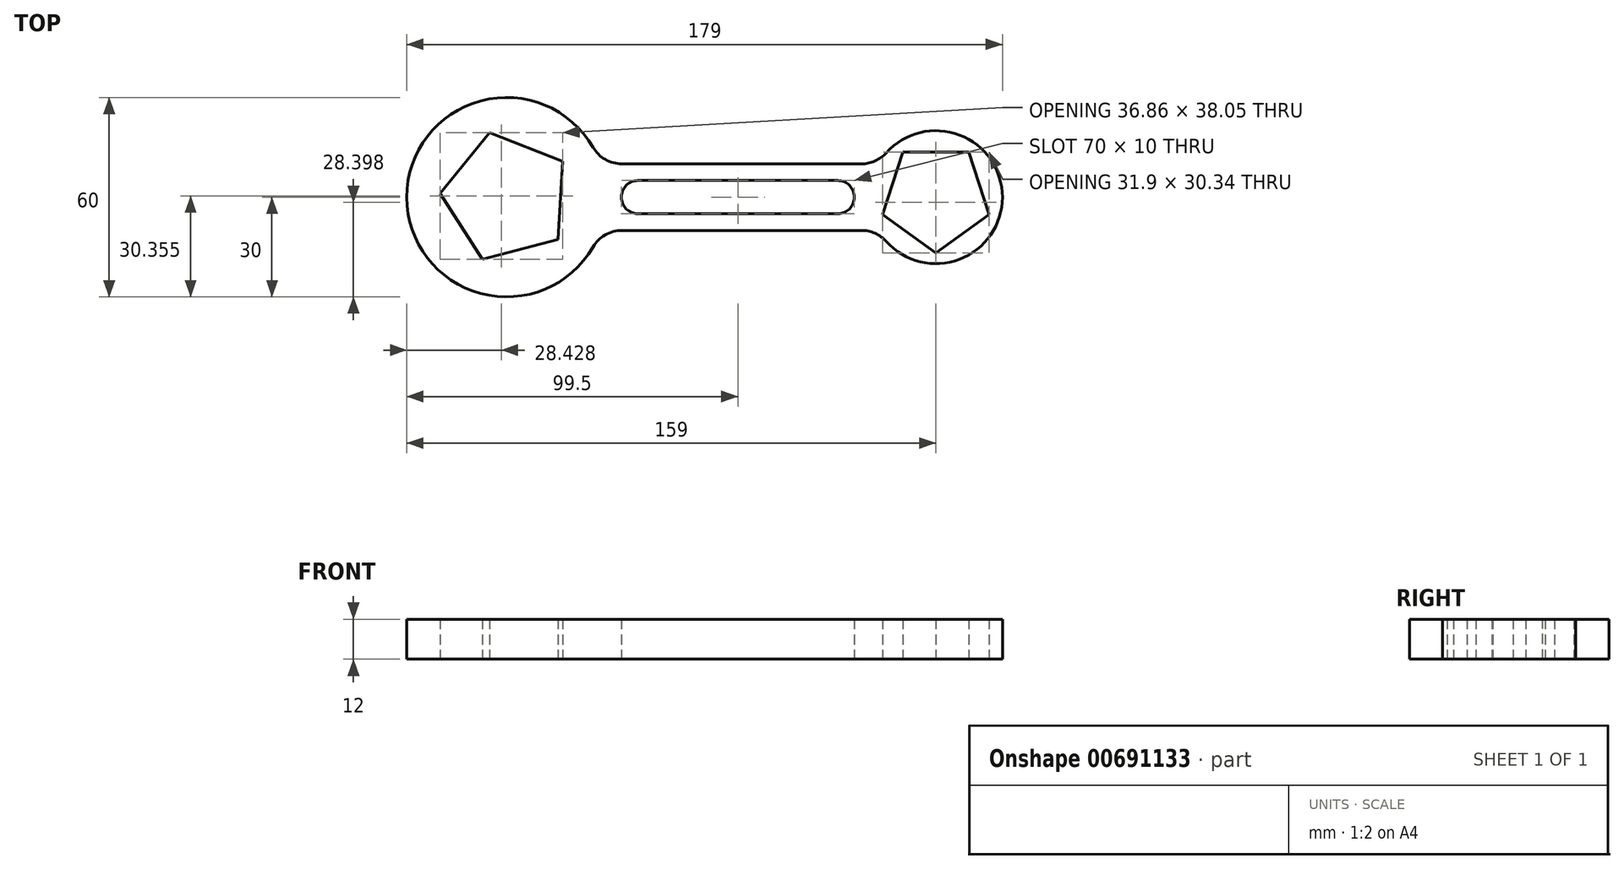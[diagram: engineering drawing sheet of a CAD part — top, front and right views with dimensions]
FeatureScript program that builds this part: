
annotation { "Feature Type Name" : "Feature", "Feature Type Description" : "" }
export const myFeature = defineFeature(function(context is Context, id is Id, definition is map)
    precondition{}
    {
        {
            var Q0;
            Q0=qCreatedBy(makeId("Top.planeOp"),FACE);
            var sketch = newSketch(context, id + "F0", { "sketchPlane" : qUnion([Q0])});
            skCircle(sketch, "E0", {"center": v(-70.3, 0) * mm, "radius": 30 * mm});
            skCircle(sketch, "E1", {"center": v(58.7, 0) * mm, "radius": 20 * mm});
            skLineSegment(sketch, "E2.bottom", {"start": v(64.5, 10) * mm, "end": v(-64.5, 10) * mm});
            skLineSegment(sketch, "E2.top", {"start": v(64.5, -10) * mm, "end": v(-64.5, -10) * mm});
            skLineSegment(sketch, "E2.left", {"start": v(64.5, 10) * mm, "end": v(64.5, -10) * mm});
            skLineSegment(sketch, "E2.right", {"start": v(-64.5, 10) * mm, "end": v(-64.5, -10) * mm});
            skPoint(sketch, "E2.middle", {"position": v(0, 0) * mm});
            skCircle(sketch, "E3.cCircle", {"center": v(-70.3, 0) * mm, "radius": 16.21 * mm, "construction": true});
            skLineSegment(sketch, "E3.0", {"start": v(-90.3, 1.15) * mm, "end": v(-75.39, 19.38) * mm});
            skLineSegment(sketch, "E3.1", {"start": v(-75.39, 19.38) * mm, "end": v(-53.44, 10.83) * mm});
            skLineSegment(sketch, "E3.2", {"start": v(-53.44, 10.83) * mm, "end": v(-54.8, -12.69) * mm});
            skLineSegment(sketch, "E3.3", {"start": v(-54.8, -12.69) * mm, "end": v(-77.57, -18.67) * mm});
            skLineSegment(sketch, "E3.4", {"start": v(-77.57, -18.67) * mm, "end": v(-90.3, 1.15) * mm});
            skPoint(sketch, "E3.0.midPoint", {"position": v(-82.85, 10.26) * mm});
            skCircle(sketch, "E4.cCircle", {"center": v(58.7, 0) * mm, "radius": 13.57 * mm, "construction": true});
            skLineSegment(sketch, "E4.0", {"start": v(48.84, 13.57) * mm, "end": v(68.56, 13.57) * mm});
            skLineSegment(sketch, "E4.1", {"start": v(68.56, 13.57) * mm, "end": v(74.65, -5.18) * mm});
            skLineSegment(sketch, "E4.2", {"start": v(74.65, -5.18) * mm, "end": v(58.7, -16.77) * mm});
            skLineSegment(sketch, "E4.3", {"start": v(58.7, -16.77) * mm, "end": v(42.75, -5.18) * mm});
            skLineSegment(sketch, "E4.4", {"start": v(42.75, -5.18) * mm, "end": v(48.84, 13.57) * mm});
            skPoint(sketch, "E4.0.midPoint", {"position": v(58.7, 13.57) * mm});
            skPoint(sketch, "E5.centerSnap0", {"position": v(-64.5, 0) * mm});
            skLineSegment(sketch, "E6.bottom", {"start": v(-53.42, 5) * mm, "end": v(53.42, 5) * mm});
            skLineSegment(sketch, "E6.top", {"start": v(-53.42, -5) * mm, "end": v(53.42, -5) * mm});
            skLineSegment(sketch, "E6.left", {"start": v(-53.42, 5) * mm, "end": v(-53.42, -5) * mm});
            skLineSegment(sketch, "E6.right", {"start": v(53.42, 5) * mm, "end": v(53.42, -5) * mm});
            skCircle(sketch, "E7", {"center": v(-30.8, 0) * mm, "radius": 5 * mm});
            skCircle(sketch, "E8", {"center": v(29.2, 0) * mm, "radius": 5 * mm});
            skSolve(sketch);
        }
        {
            var Q0;
            Q0=makeQuery(id+"F0.imprint","IMPRINT",FACE,{"disambiguationData":[TD([[makeQuery(id+"F0.imprint","IMPRINT",EDGE,{"derivedFrom":sQuery(id+"F0.wireOp",EDGE,"E3.0")}),1.0]])]});
            var Q1;
            {var subQ12=sQuery(id+"F0.wireOp",EDGE,"E6.left");Q1=makeQuery(id+"F0.imprint","IMPRINT",FACE,{"disambiguationData":[TD([[makeQuery(id+"F0.imprint","IMPRINT",EDGE,{"derivedFrom":subQ12}),-1.0]])]});}
            var Q2;
            {var subQ5=sQuery(id+"F0.wireOp",EDGE,"E6.left");Q2=makeQuery(id+"F0.imprint","IMPRINT",FACE,{"disambiguationData":[TD([[makeQuery(id+"F0.imprint","IMPRINT",EDGE,{"derivedFrom":subQ5}),1.0]])]});}
            var Q3;
            {var subQ1=sQuery(id+"F0.wireOp",EDGE,"E0");var subQ4=sQuery(id+"F0.wireOp",EDGE,"E2.bottom");var subQ8=makeQuery(id+"F0.imprint","INTERSECT",VERTEX,{"derivedFrom":[subQ1,subQ4]});Q3=makeQuery(id+"F0.imprint","IMPRINT",FACE,{"disambiguationData":[TD([[makeQuery(id+"F0.imprint","IMPRINT",EDGE,{"disambiguationData":[TD([[subQ8,1.0]])],"derivedFrom":subQ1}),-1.0]])]});}
            var Q4;
            {var subQ0=sQuery(id+"F0.wireOp",EDGE,"E6.bottom");var subQ1=sQuery(id+"F0.wireOp",EDGE,"E0");var subQ2=makeQuery(id+"F0.imprint","INTERSECT",VERTEX,{"derivedFrom":[subQ1,subQ0]});Q4=makeQuery(id+"F0.imprint","IMPRINT",FACE,{"disambiguationData":[TD([[makeQuery(id+"F0.imprint","IMPRINT",EDGE,{"disambiguationData":[TD([[subQ2,1.0]])],"derivedFrom":subQ1}),-1.0]])]});}
            var Q5;
            {var subQ1=sQuery(id+"F0.wireOp",EDGE,"E0");var subQ4=sQuery(id+"F0.wireOp",EDGE,"E2.top");var subQ5=makeQuery(id+"F0.imprint","INTERSECT",VERTEX,{"derivedFrom":[subQ1,subQ4]});Q5=makeQuery(id+"F0.imprint","IMPRINT",FACE,{"disambiguationData":[TD([[makeQuery(id+"F0.imprint","IMPRINT",EDGE,{"disambiguationData":[TD([[subQ5,-1.0]])],"derivedFrom":subQ1}),-1.0]])]});}
            var Q6;
            {var subQ0=sQuery(id+"F0.wireOp",EDGE,"E6.bottom");var subQ1=sQuery(id+"F0.wireOp",EDGE,"E1");var subQ2=makeQuery(id+"F0.imprint","INTERSECT",VERTEX,{"derivedFrom":[subQ1,subQ0]});Q6=makeQuery(id+"F0.imprint","IMPRINT",FACE,{"disambiguationData":[TD([[makeQuery(id+"F0.imprint","IMPRINT",EDGE,{"disambiguationData":[TD([[subQ2,-1.0]])],"derivedFrom":subQ1}),-1.0]])]});}
            var Q7;
            {var subQ0=sQuery(id+"F0.wireOp",EDGE,"E2.bottom");var subQ1=sQuery(id+"F0.wireOp",EDGE,"E1");var subQ2=makeQuery(id+"F0.imprint","INTERSECT",VERTEX,{"derivedFrom":[subQ1,subQ0]});Q7=makeQuery(id+"F0.imprint","IMPRINT",FACE,{"disambiguationData":[TD([[makeQuery(id+"F0.imprint","IMPRINT",EDGE,{"disambiguationData":[TD([[subQ2,-1.0]])],"derivedFrom":subQ1}),1.0]])]});}
            var Q8;
            {var subQ9=sQuery(id+"F0.wireOp",EDGE,"E4.0");Q8=makeQuery(id+"F0.imprint","IMPRINT",FACE,{"disambiguationData":[TD([[makeQuery(id+"F0.imprint","IMPRINT",EDGE,{"derivedFrom":subQ9}),1.0]])]});}
            var Q9;
            {var subQ0=sQuery(id+"F0.wireOp",EDGE,"E6.bottom");var subQ1=sQuery(id+"F0.wireOp",EDGE,"E1");var subQ2=makeQuery(id+"F0.imprint","INTERSECT",VERTEX,{"derivedFrom":[subQ1,subQ0]});Q9=makeQuery(id+"F0.imprint","IMPRINT",FACE,{"disambiguationData":[TD([[makeQuery(id+"F0.imprint","IMPRINT",EDGE,{"disambiguationData":[TD([[subQ2,-1.0]])],"derivedFrom":subQ1}),1.0]])]});}
            var Q10;
            {var subQ5=sQuery(id+"F0.wireOp",EDGE,"E2.top");var subQ6=sQuery(id+"F0.wireOp",EDGE,"E1");var subQ7=makeQuery(id+"F0.imprint","INTERSECT",VERTEX,{"derivedFrom":[subQ6,subQ5]});Q10=makeQuery(id+"F0.imprint","IMPRINT",FACE,{"disambiguationData":[TD([[makeQuery(id+"F0.imprint","IMPRINT",EDGE,{"disambiguationData":[TD([[subQ7,1.0]])],"derivedFrom":subQ6}),1.0]])]});}
            extrude(context, id + "F1", {"entities" : qUnion([Q0, Q1, Q2, Q3, Q4, Q5, Q6, Q7, Q8, Q9, Q10]), "depth" : 12 * mm, "offsetDistance" : 25 * mm});
        }
        {
            var Q0;
            Q0=makeQuery(id+"F1.opExtrude","SWEPT_EDGE",EDGE,{"disambiguationData":[OSD([sQuery(id+"F0.wireOp",EDGE,"E1"),sQuery(id+"F0.wireOp",EDGE,"E2.top")])]});
            var Q1;
            Q1=makeQuery(id+"F1.opExtrude","SWEPT_EDGE",EDGE,{"disambiguationData":[OSD([sQuery(id+"F0.wireOp",EDGE,"E0"),sQuery(id+"F0.wireOp",EDGE,"E2.top")])]});
            var Q2;
            Q2=makeQuery(id+"F1.opExtrude","SWEPT_EDGE",EDGE,{"disambiguationData":[OSD([sQuery(id+"F0.wireOp",EDGE,"E1"),sQuery(id+"F0.wireOp",EDGE,"E2.bottom")])]});
            var Q3;
            Q3=makeQuery(id+"F1.opExtrude","SWEPT_EDGE",EDGE,{"disambiguationData":[OSD([sQuery(id+"F0.wireOp",EDGE,"E0"),sQuery(id+"F0.wireOp",EDGE,"E2.bottom")])]});
            fillet(context, id + "F2", {"entities" : qUnion([Q0, Q1, Q2, Q3]), "radius" : 10 * mm, "tangentPropagation" : true, "allowEdgeOverflow" : false});
        }
    });
